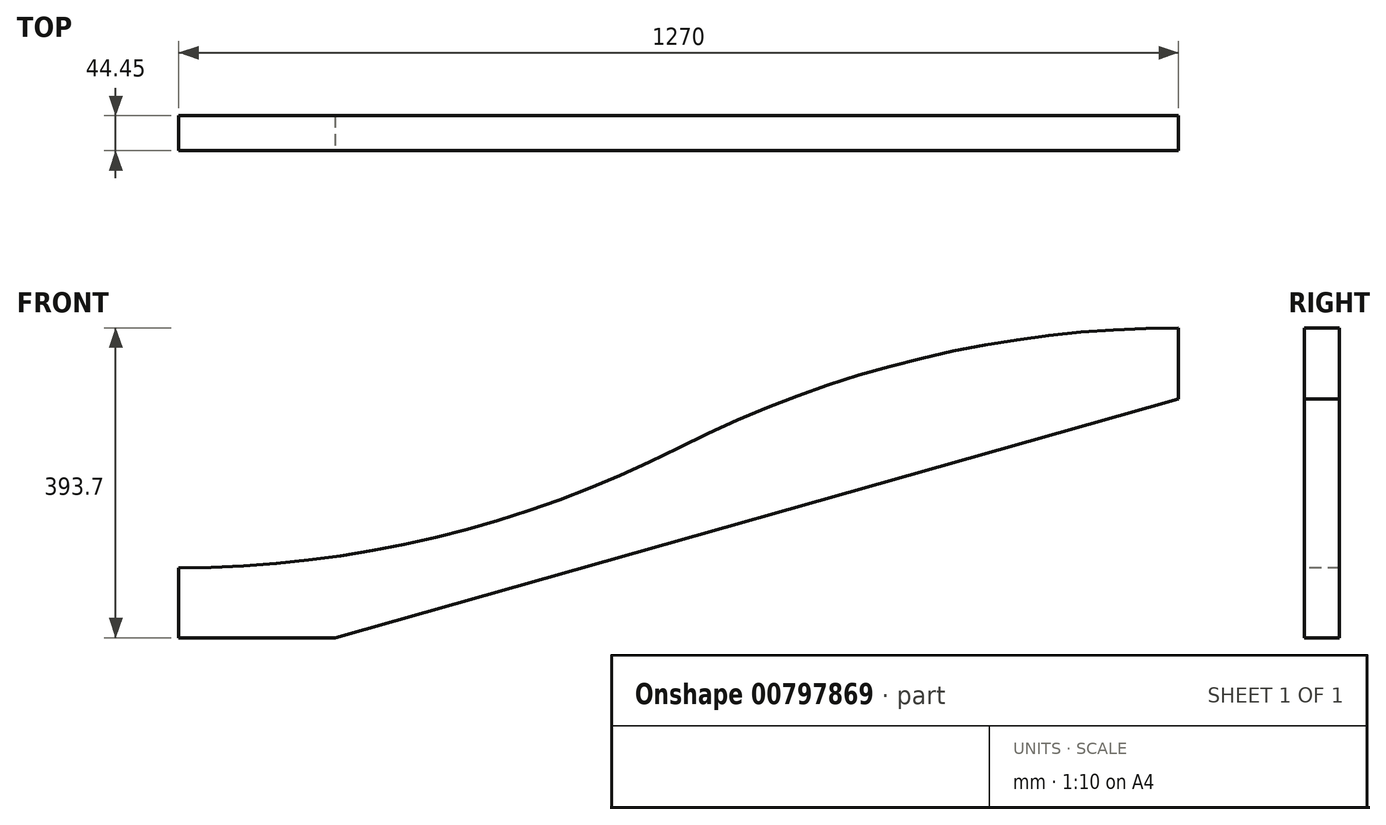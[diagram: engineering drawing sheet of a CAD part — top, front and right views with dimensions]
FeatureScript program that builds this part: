
annotation { "Feature Type Name" : "Feature", "Feature Type Description" : "" }
export const myFeature = defineFeature(function(context is Context, id is Id, definition is map)
    precondition{}
    {
        {
            var Q0;
            Q0=qCreatedBy(makeId("Front.planeOp"),FACE);
            var sketch = newSketch(context, id + "F0", { "sketchPlane" : qUnion([Q0])});
            skLineSegment(sketch, "E0.bottom", {"start": v(0, 0) * mm, "end": v(1270, 0) * mm});
            skLineSegment(sketch, "E0.top", {"start": v(0, 393.7) * mm, "end": v(1270, 393.7) * mm});
            skLineSegment(sketch, "E0.left", {"start": v(0, 0) * mm, "end": v(0, 393.7) * mm});
            skLineSegment(sketch, "E0.right", {"start": v(1270, 0) * mm, "end": v(1270, 393.7) * mm});
            skLineSegment(sketch, "E1", {"start": v(0, 88.9) * mm, "end": v(1270, 88.9) * mm});
            skArc(sketch, "E2", {"start": v(0, 88.9) * mm, "mid": v(326.52, 127.53) * mm, "end": v(635, 241.3) * mm});
            skArc(sketch, "E3", {"start": v(1270, 393.7) * mm, "mid": v(943.48, 355.07) * mm, "end": v(635, 241.3) * mm});
            skLineSegment(sketch, "E4", {"start": v(0, 88.9) * mm, "end": v(1270, 448.8) * mm});
            skLineSegment(sketch, "E5", {"start": v(0, -56.3) * mm, "end": v(1270, 303.6) * mm});
            skLineSegment(sketch, "E6", {"start": v(1270, 448.8) * mm, "end": v(1270, 303.6) * mm});
            skLineSegment(sketch, "E7", {"start": v(0, 88.9) * mm, "end": v(0, -56.3) * mm});
            skSolve(sketch);
        }
        {
            var Q0;
            {var subQ1=sQuery(id+"F0.wireOp",EDGE,"E2");Q0=makeQuery(id+"F0.imprint","IMPRINT",FACE,{"disambiguationData":[TD([[makeQuery(id+"F0.imprint","IMPRINT",EDGE,{"derivedFrom":subQ1}),-1.0]])]});}
            var Q1;
            {var subQ0=sQuery(id+"F0.wireOp",EDGE,"E7");var subQ1=sQuery(id+"F0.wireOp",EDGE,"E0.bottom");var subQ2=makeQuery(id+"F0.imprint","INTERSECT",VERTEX,{"derivedFrom":[subQ1,subQ0]});Q1=makeQuery(id+"F0.imprint","IMPRINT",FACE,{"disambiguationData":[TD([[makeQuery(id+"F0.imprint","IMPRINT",EDGE,{"disambiguationData":[TD([[subQ2,-1.0]])],"derivedFrom":subQ1}),1.0]])]});}
            extrude(context, id + "F1", {"entities" : qUnion([Q0, Q1]), "oppositeDirection" : true, "depth" : 44.45 * mm, "offsetDistance" : 25.4 * mm});
        }
    });
